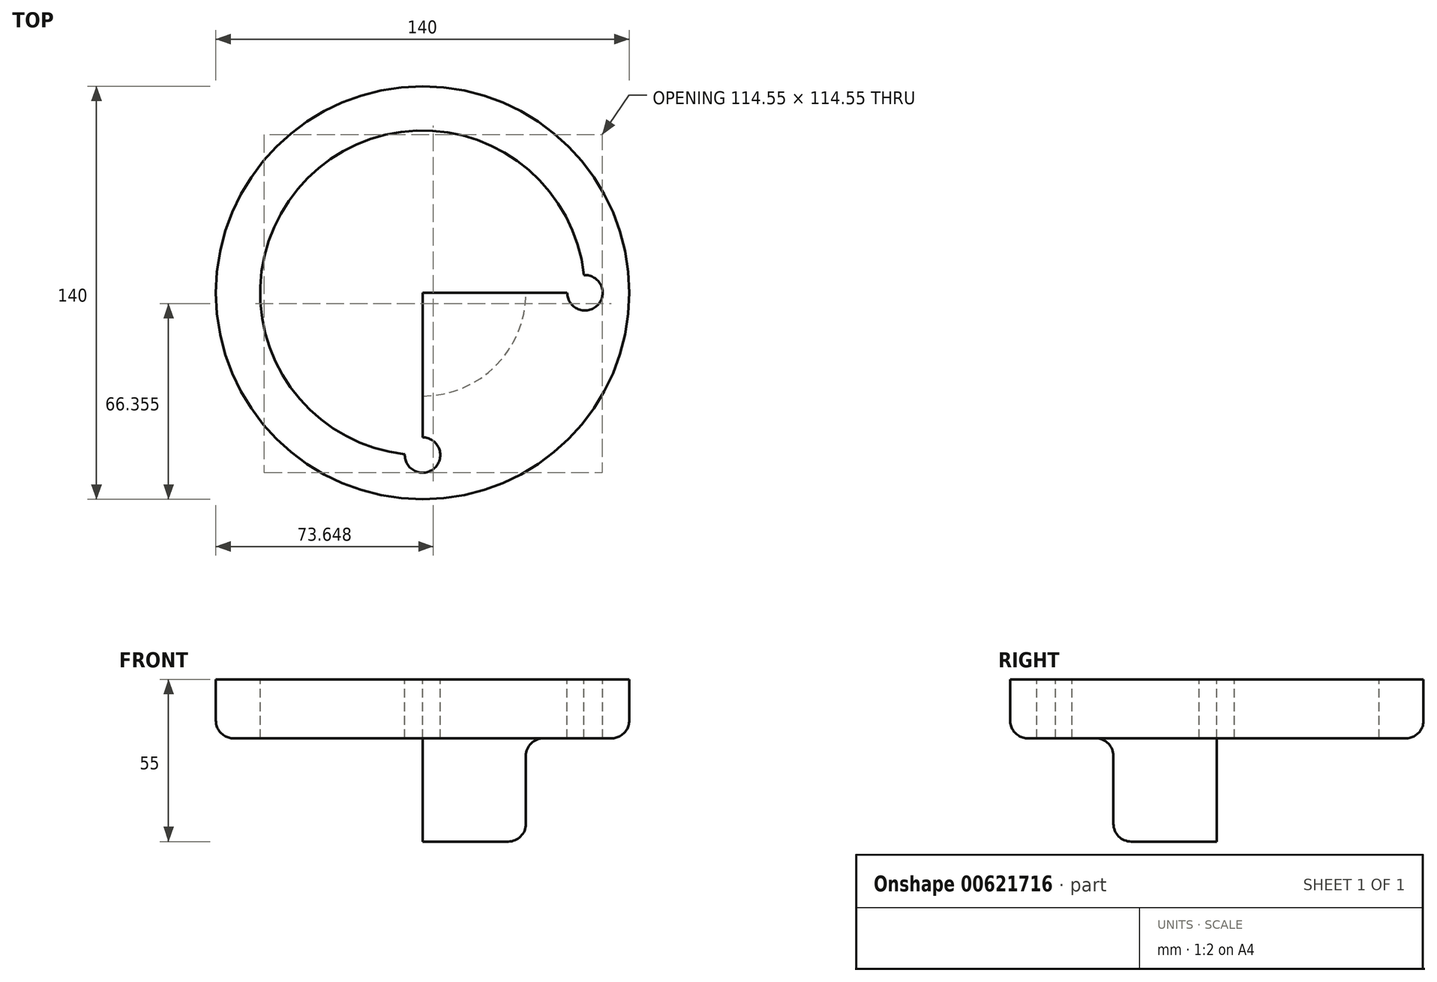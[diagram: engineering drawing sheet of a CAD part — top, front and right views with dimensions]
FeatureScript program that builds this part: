
annotation { "Feature Type Name" : "Feature", "Feature Type Description" : "" }
export const myFeature = defineFeature(function(context is Context, id is Id, definition is map)
    precondition{}
    {
        {
            var Q0;
            Q0=qCreatedBy(makeId("Front.planeOp"),FACE);
            var sketch = newSketch(context, id + "F0", { "sketchPlane" : qUnion([Q0])});
            skLineSegment(sketch, "E0", {"start": v(-49.17, 29.71) * mm, "end": v(20.83, 29.71) * mm});
            skLineSegment(sketch, "E1", {"start": v(-49.17, 29.71) * mm, "end": v(-49.17, 15.71) * mm});
            skLineSegment(sketch, "E2", {"start": v(20.83, 29.71) * mm, "end": v(20.83, -25.29) * mm});
            skLineSegment(sketch, "E3", {"start": v(20.83, -25.29) * mm, "end": v(-8.17, -25.29) * mm});
            skLineSegment(sketch, "E4", {"start": v(-43.17, 9.71) * mm, "end": v(-20.17, 9.71) * mm});
            skLineSegment(sketch, "E5", {"start": v(-14.17, 3.71) * mm, "end": v(-14.17, -19.29) * mm});
            skPoint(sketch, "E6.visualSharp", {"position": v(-14.17, 9.71) * mm});
            skArc(sketch, "E6.filletArc", {"start": v(-14.17, 3.71) * mm, "mid": v(-15.93, 7.95) * mm, "end": v(-20.17, 9.71) * mm});
            skPoint(sketch, "E7.visualSharp", {"position": v(-14.17, -25.29) * mm});
            skArc(sketch, "E7.filletArc", {"start": v(-14.17, -19.29) * mm, "mid": v(-12.41, -23.53) * mm, "end": v(-8.17, -25.29) * mm});
            skPoint(sketch, "E8.visualSharp", {"position": v(-49.17, 9.71) * mm});
            skArc(sketch, "E8.filletArc", {"start": v(-49.17, 15.71) * mm, "mid": v(-47.41, 11.47) * mm, "end": v(-43.17, 9.71) * mm});
            skSolve(sketch);
        }
        {
            var Q0;
            Q0=makeQuery(id+"F0.imprint","IMPRINT",FACE,{"disambiguationData":[TD([[makeQuery(id+"F0.imprint","IMPRINT",EDGE,{"derivedFrom":sQuery(id+"F0.wireOp",EDGE,"E0")}),-1.0]])]});
            var Q1;
            Q1=sQuery(id+"F0.wireOp",EDGE,"E2");
            revolve(context, id + "F1", {"entities" : qUnion([Q0]), "axis" : qUnion([Q1]), "revolveType" : RevolveType.FULL});
        }
        {
            var Q0;
            Q0=makeQuery(id+"F1.opRevolve","SWEPT_FACE",FACE,{"disambiguationData":[OSD([sQuery(id+"F0.wireOp",EDGE,"E0")])]});
            var sketch = newSketch(context, id + "F2", { "sketchPlane" : qUnion([Q0])});
            skLineSegment(sketch, "E9", {"start": v(-49.17, 0) * mm, "end": v(90.83, 0) * mm});
            skLineSegment(sketch, "E10", {"start": v(20.83, 70) * mm, "end": v(20.83, -70) * mm});
            skPoint(sketch, "E10.startSnap0", {"position": v(20.83, 0) * mm});
            skCircle(sketch, "E11", {"center": v(20.83, 0) * mm, "radius": 55 * mm});
            skCircle(sketch, "E12", {"center": v(-34.17, 0) * mm, "radius": 6 * mm});
            skCircle(sketch, "E13", {"center": v(20.83, -55) * mm, "radius": 6 * mm});
            skCircle(sketch, "E14", {"center": v(75.83, 0) * mm, "radius": 6 * mm});
            skCircle(sketch, "E15", {"center": v(20.83, 55) * mm, "radius": 6 * mm});
            skSolve(sketch);
        }
        {
            var Q0;
            {var subQ0=sQuery(id+"F2.wireOp",EDGE,"E15");var subQ1=sQuery(id+"F2.wireOp",EDGE,"E10");var subQ2=makeQuery(id+"F2.imprint","INTERSECT",VERTEX,{"disambiguationData":[OD(0.0)],"derivedFrom":[subQ1,subQ0]});Q0=makeQuery(id+"F2.imprint","IMPRINT",FACE,{"disambiguationData":[TD([[makeQuery(id+"F2.imprint","IMPRINT",EDGE,{"disambiguationData":[TD([[subQ2,-1.0]])],"derivedFrom":subQ1}),1.0]])]});}
            var Q1;
            {var subQ0=sQuery(id+"F2.wireOp",EDGE,"E15");var subQ1=sQuery(id+"F2.wireOp",EDGE,"E10");var subQ2=makeQuery(id+"F2.imprint","INTERSECT",VERTEX,{"disambiguationData":[OD(0.0)],"derivedFrom":[subQ1,subQ0]});Q1=makeQuery(id+"F2.imprint","IMPRINT",FACE,{"disambiguationData":[TD([[makeQuery(id+"F2.imprint","IMPRINT",EDGE,{"disambiguationData":[TD([[subQ2,-1.0]])],"derivedFrom":subQ1}),-1.0]])]});}
            var Q2;
            {var subQ0=sQuery(id+"F2.wireOp",EDGE,"E11");var subQ1=sQuery(id+"F2.wireOp",EDGE,"E10");var subQ2=makeQuery(id+"F2.imprint","INTERSECT",VERTEX,{"disambiguationData":[OD(0.0)],"derivedFrom":[subQ1,subQ0]});Q2=makeQuery(id+"F2.imprint","IMPRINT",FACE,{"disambiguationData":[TD([[makeQuery(id+"F2.imprint","IMPRINT",EDGE,{"disambiguationData":[TD([[subQ2,-1.0]])],"derivedFrom":subQ1}),-1.0]])]});}
            var Q3;
            {var subQ0=sQuery(id+"F2.wireOp",EDGE,"E11");var subQ1=sQuery(id+"F2.wireOp",EDGE,"E10");var subQ2=makeQuery(id+"F2.imprint","INTERSECT",VERTEX,{"disambiguationData":[OD(0.0)],"derivedFrom":[subQ1,subQ0]});Q3=makeQuery(id+"F2.imprint","IMPRINT",FACE,{"disambiguationData":[TD([[makeQuery(id+"F2.imprint","IMPRINT",EDGE,{"disambiguationData":[TD([[subQ2,-1.0]])],"derivedFrom":subQ1}),1.0]])]});}
            var Q4;
            {var subQ0=sQuery(id+"F2.wireOp",EDGE,"E11");var subQ1=sQuery(id+"F2.wireOp",EDGE,"E9");var subQ2=makeQuery(id+"F2.imprint","INTERSECT",VERTEX,{"disambiguationData":[OD(0.0)],"derivedFrom":[subQ1,subQ0]});Q4=makeQuery(id+"F2.imprint","IMPRINT",FACE,{"disambiguationData":[TD([[makeQuery(id+"F2.imprint","IMPRINT",EDGE,{"disambiguationData":[TD([[subQ2,-1.0]])],"derivedFrom":subQ1}),-1.0]])]});}
            var Q5;
            {var subQ0=sQuery(id+"F2.wireOp",EDGE,"E11");var subQ1=sQuery(id+"F2.wireOp",EDGE,"E9");var subQ2=makeQuery(id+"F2.imprint","INTERSECT",VERTEX,{"disambiguationData":[OD(0.0)],"derivedFrom":[subQ1,subQ0]});Q5=makeQuery(id+"F2.imprint","IMPRINT",FACE,{"disambiguationData":[TD([[makeQuery(id+"F2.imprint","IMPRINT",EDGE,{"disambiguationData":[TD([[subQ2,-1.0]])],"derivedFrom":subQ1}),1.0]])]});}
            var Q6;
            {var subQ0=sQuery(id+"F2.wireOp",EDGE,"E12");var subQ1=sQuery(id+"F2.wireOp",EDGE,"E9");var subQ2=makeQuery(id+"F2.imprint","INTERSECT",VERTEX,{"disambiguationData":[OD(0.0)],"derivedFrom":[subQ1,subQ0]});Q6=makeQuery(id+"F2.imprint","IMPRINT",FACE,{"disambiguationData":[TD([[makeQuery(id+"F2.imprint","IMPRINT",EDGE,{"disambiguationData":[TD([[subQ2,-1.0]])],"derivedFrom":subQ1}),1.0]])]});}
            var Q7;
            {var subQ0=sQuery(id+"F2.wireOp",EDGE,"E12");var subQ1=sQuery(id+"F2.wireOp",EDGE,"E9");var subQ2=makeQuery(id+"F2.imprint","INTERSECT",VERTEX,{"disambiguationData":[OD(0.0)],"derivedFrom":[subQ1,subQ0]});Q7=makeQuery(id+"F2.imprint","IMPRINT",FACE,{"disambiguationData":[TD([[makeQuery(id+"F2.imprint","IMPRINT",EDGE,{"disambiguationData":[TD([[subQ2,-1.0]])],"derivedFrom":subQ1}),-1.0]])]});}
            var Q8;
            {var subQ0=sQuery(id+"F2.wireOp",EDGE,"E11");var subQ1=sQuery(id+"F2.wireOp",EDGE,"E10");var subQ2=makeQuery(id+"F2.imprint","INTERSECT",VERTEX,{"disambiguationData":[OD(1.0)],"derivedFrom":[subQ1,subQ0]});Q8=makeQuery(id+"F2.imprint","IMPRINT",FACE,{"disambiguationData":[TD([[makeQuery(id+"F2.imprint","IMPRINT",EDGE,{"disambiguationData":[TD([[subQ2,-1.0]])],"derivedFrom":subQ1}),-1.0]])]});}
            var Q9;
            {var subQ0=sQuery(id+"F2.wireOp",EDGE,"E13");var subQ1=sQuery(id+"F2.wireOp",EDGE,"E10");var subQ2=makeQuery(id+"F2.imprint","INTERSECT",VERTEX,{"disambiguationData":[OD(0.0)],"derivedFrom":[subQ1,subQ0]});Q9=makeQuery(id+"F2.imprint","IMPRINT",FACE,{"disambiguationData":[TD([[makeQuery(id+"F2.imprint","IMPRINT",EDGE,{"disambiguationData":[TD([[subQ2,-1.0]])],"derivedFrom":subQ1}),-1.0]])]});}
            var Q10;
            {var subQ0=sQuery(id+"F2.wireOp",EDGE,"E11");var subQ1=sQuery(id+"F2.wireOp",EDGE,"E10");var subQ2=makeQuery(id+"F2.imprint","INTERSECT",VERTEX,{"disambiguationData":[OD(1.0)],"derivedFrom":[subQ1,subQ0]});Q10=makeQuery(id+"F2.imprint","IMPRINT",FACE,{"disambiguationData":[TD([[makeQuery(id+"F2.imprint","IMPRINT",EDGE,{"disambiguationData":[TD([[subQ2,-1.0]])],"derivedFrom":subQ1}),1.0]])]});}
            var Q11;
            {var subQ0=sQuery(id+"F2.wireOp",EDGE,"E13");var subQ1=sQuery(id+"F2.wireOp",EDGE,"E10");var subQ2=makeQuery(id+"F2.imprint","INTERSECT",VERTEX,{"disambiguationData":[OD(0.0)],"derivedFrom":[subQ1,subQ0]});Q11=makeQuery(id+"F2.imprint","IMPRINT",FACE,{"disambiguationData":[TD([[makeQuery(id+"F2.imprint","IMPRINT",EDGE,{"disambiguationData":[TD([[subQ2,-1.0]])],"derivedFrom":subQ1}),1.0]])]});}
            var Q12;
            {var subQ0=sQuery(id+"F2.wireOp",EDGE,"E11");var subQ1=sQuery(id+"F2.wireOp",EDGE,"E9");var subQ2=makeQuery(id+"F2.imprint","INTERSECT",VERTEX,{"disambiguationData":[OD(1.0)],"derivedFrom":[subQ1,subQ0]});Q12=makeQuery(id+"F2.imprint","IMPRINT",FACE,{"disambiguationData":[TD([[makeQuery(id+"F2.imprint","IMPRINT",EDGE,{"disambiguationData":[TD([[subQ2,-1.0]])],"derivedFrom":subQ1}),-1.0]])]});}
            var Q13;
            {var subQ0=sQuery(id+"F2.wireOp",EDGE,"E14");var subQ1=sQuery(id+"F2.wireOp",EDGE,"E9");var subQ2=makeQuery(id+"F2.imprint","INTERSECT",VERTEX,{"disambiguationData":[OD(0.0)],"derivedFrom":[subQ1,subQ0]});Q13=makeQuery(id+"F2.imprint","IMPRINT",FACE,{"disambiguationData":[TD([[makeQuery(id+"F2.imprint","IMPRINT",EDGE,{"disambiguationData":[TD([[subQ2,-1.0]])],"derivedFrom":subQ1}),-1.0]])]});}
            var Q14;
            {var subQ0=sQuery(id+"F2.wireOp",EDGE,"E14");var subQ1=sQuery(id+"F2.wireOp",EDGE,"E9");var subQ2=makeQuery(id+"F2.imprint","INTERSECT",VERTEX,{"disambiguationData":[OD(0.0)],"derivedFrom":[subQ1,subQ0]});Q14=makeQuery(id+"F2.imprint","IMPRINT",FACE,{"disambiguationData":[TD([[makeQuery(id+"F2.imprint","IMPRINT",EDGE,{"disambiguationData":[TD([[subQ2,-1.0]])],"derivedFrom":subQ1}),1.0]])]});}
            var Q15;
            {var subQ0=sQuery(id+"F2.wireOp",EDGE,"E11");var subQ1=sQuery(id+"F2.wireOp",EDGE,"E9");var subQ2=makeQuery(id+"F2.imprint","INTERSECT",VERTEX,{"disambiguationData":[OD(1.0)],"derivedFrom":[subQ1,subQ0]});Q15=makeQuery(id+"F2.imprint","IMPRINT",FACE,{"disambiguationData":[TD([[makeQuery(id+"F2.imprint","IMPRINT",EDGE,{"disambiguationData":[TD([[subQ2,-1.0]])],"derivedFrom":subQ1}),1.0]])]});}
            extrude(context, id + "F3", {"entities" : qUnion([Q0, Q1, Q2, Q3, Q4, Q5, Q6, Q7, Q8, Q9, Q10, Q11, Q12, Q13, Q14, Q15]), "operationType" : NewBodyOperationType.REMOVE, "endBound" : BoundingType.THROUGH_ALL, "oppositeDirection" : true, "depth" : 25 * mm, "offsetDistance" : 25 * mm});
        }
    });
